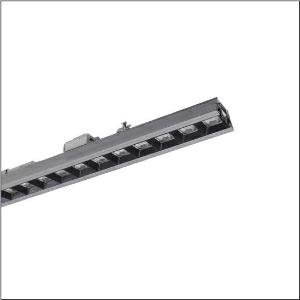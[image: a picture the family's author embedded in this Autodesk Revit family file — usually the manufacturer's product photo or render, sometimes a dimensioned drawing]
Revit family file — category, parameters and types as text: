
# Revit family: licross_r__21_silica_51ts12dn4zm00583xx_641b
name_source: partatom
category: Lighting Fixtures
units: mm (PartAtom-declared; Revit-internal decimal feet)

## family parameters
Cut with Voids When Loaded = No
Host = Face
Light Source = No
Part Type = Normal
Room Calculation Point = No
Round Connector Dimension = Use Diameter
Shared = No

## types (1)
- --- (1 x LED, 6340 lm, 39 W, 4000K)
    Apparent Load = 39 VA
    CIE Flux Codes = 86 100 100 100 100
    Color Rendering = 80
    Color Temperature = 4000K
    Default Elevation = 1800 mm
    Description = Licross® 21 Silica, luminaire insert, of sheet steel, galvanised, coil coated, silver, length: 1.500mm, width: 82mm, height: 86mm, LED rated luminous flux: 6.340lm, light colour: 840, control gear: DALI 2, with plug, 5-pole, with phase selection, mains connection: 220..240V, AC, 50/60Hz, rated input power: 39W, halogen-free wiring, primary light control with lens, of PMMA, primary anti-glare with darklight reflector, of PC, CAT 2 (L<= 1000cd/m²), light emission: direct distribution, primary light characteristic: symmetric, protection rating (complete): IP40, insulation class (complete): insulation class I (protective earthing), certification: CE, UKCA, protection symbol: D if used in an environment without relevant dust loads, impact resistance: IK03, permissible ambient temperature for indoor applications: -25..+45°C, corresponds to IFS (International Featured Standards) requirements for safety and quality in the food industry, reducing of maximum allowable ambient temperature of 5°C with ceiling mounting, LABS conformity tested according to VDMA 24364:2018-05, packaging unit: 1 piece
    Height = 86 mm
    Lamp = 1 x LED
    Lamp Light Flux = 6340 lm
    Lamp Power = 39 W
    Lamp count = 1
    Length = 1500 mm
    Luminous efficacy = 163 lm/W
    Manufacturer = Siteco
    ModVariant = No
    Model = 51TS12DN4ZM00583XX
    Mounting Place = Ceiling
    Mounting Type = Pendant
    Number of Poles = 1
    OnlyDefault = Yes
    Power Factor = 1
    Product Name = Licross® 21 Silica
    Product group = luminaire insert
    ProductGroupID = 901
    Protection Class = Protection class I
    Protection Degree = IP 40
    RLX_Detail_Level = 1
    RLX_Emergency_Light_Flux = 0 lm
    RLX_Emergency_Type = 0
    RLX_Emergency_Type_DB = No
    RlxData = <blob elided: 57165 chars, md5=7ed955c1>
    Socket = socket
    Standby Power = 0 W
    System Light Flux = 6340 lm
    System Power = 39 W
    Type Comments = factory setting: luminous flux: 100 % | dim-lin: 254 | 435 mA
    Type Image = l_1290833.jpg
    URL = http://relux.com
    VarID = @adj_036521
    Voltage = 0 V
    Weight = 0.00 kg
    Width = 82 mm  [stored 0.269029 ft]

note: [stored X ft] marks values corroborated as IEEE doubles in the binary element streams (Revit-internal decimal feet)

## geometry (parser evidence)
native form markers: Blend x4, Sweep x10
no freeform markers — native parametric forms only
